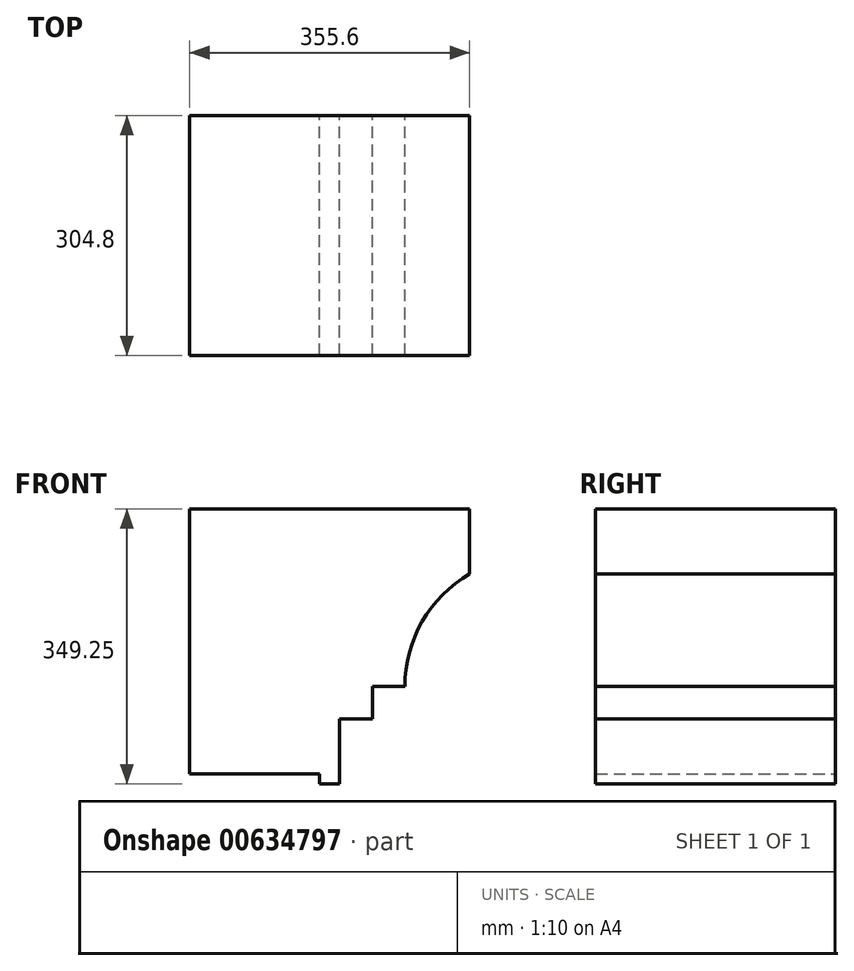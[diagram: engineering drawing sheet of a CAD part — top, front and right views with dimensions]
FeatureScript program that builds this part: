
annotation { "Feature Type Name" : "Feature", "Feature Type Description" : "" }
export const myFeature = defineFeature(function(context is Context, id is Id, definition is map)
    precondition{}
    {
        {
            var Q0;
            Q0=qCreatedBy(makeId("Front.planeOp"),FACE);
            var sketch = newSketch(context, id + "F0", { "sketchPlane" : qUnion([Q0])});
            skLineSegment(sketch, "E0", {"start": v(273.14, -225.38) * mm, "end": v(231.82, -225.38) * mm});
            skLineSegment(sketch, "E1", {"start": v(231.82, -225.38) * mm, "end": v(231.82, -266.7) * mm});
            skLineSegment(sketch, "E2", {"start": v(231.82, -266.7) * mm, "end": v(190.5, -266.7) * mm});
            skLineSegment(sketch, "E3", {"start": v(190.5, -266.7) * mm, "end": v(190.5, -349.25) * mm});
            skLineSegment(sketch, "E4", {"start": v(0, 0) * mm, "end": v(355.6, 0) * mm});
            skLineSegment(sketch, "E5", {"start": v(355.6, 0) * mm, "end": v(355.6, -82.55) * mm});
            skArc(sketch, "E6", {"start": v(355.6, -82.55) * mm, "mid": v(295.23, -142.92) * mm, "end": v(273.14, -225.38) * mm});
            skLineSegment(sketch, "E7", {"start": v(273.14, -225.38) * mm, "end": v(438.06, -225.38) * mm, "construction": true});
            skPoint(sketch, "E8", {"position": v(355.6, -225.38) * mm});
            skLineSegment(sketch, "E9", {"start": v(0, -336.55) * mm, "end": v(0, -336.55) * mm});
            skLineSegment(sketch, "E10", {"start": v(0, -336.55) * mm, "end": v(0, 0) * mm});
            skLineSegment(sketch, "E11", {"start": v(190.5, -349.25) * mm, "end": v(165.1, -349.25) * mm});
            skLineSegment(sketch, "E12", {"start": v(165.1, -349.25) * mm, "end": v(165.1, -336.55) * mm});
            skLineSegment(sketch, "E13", {"start": v(165.1, -336.55) * mm, "end": v(0, -336.55) * mm});
            skSolve(sketch);
        }
        {
            var Q0;
            Q0 = qSketchRegion(id + "F0", true);
            extrude(context, id + "F1", {"entities" : qUnion([Q0]), "endBound" : BoundingType.SYMMETRIC, "depth" : 304.8 * mm, "offsetDistance" : 25.4 * mm});
        }
    });
